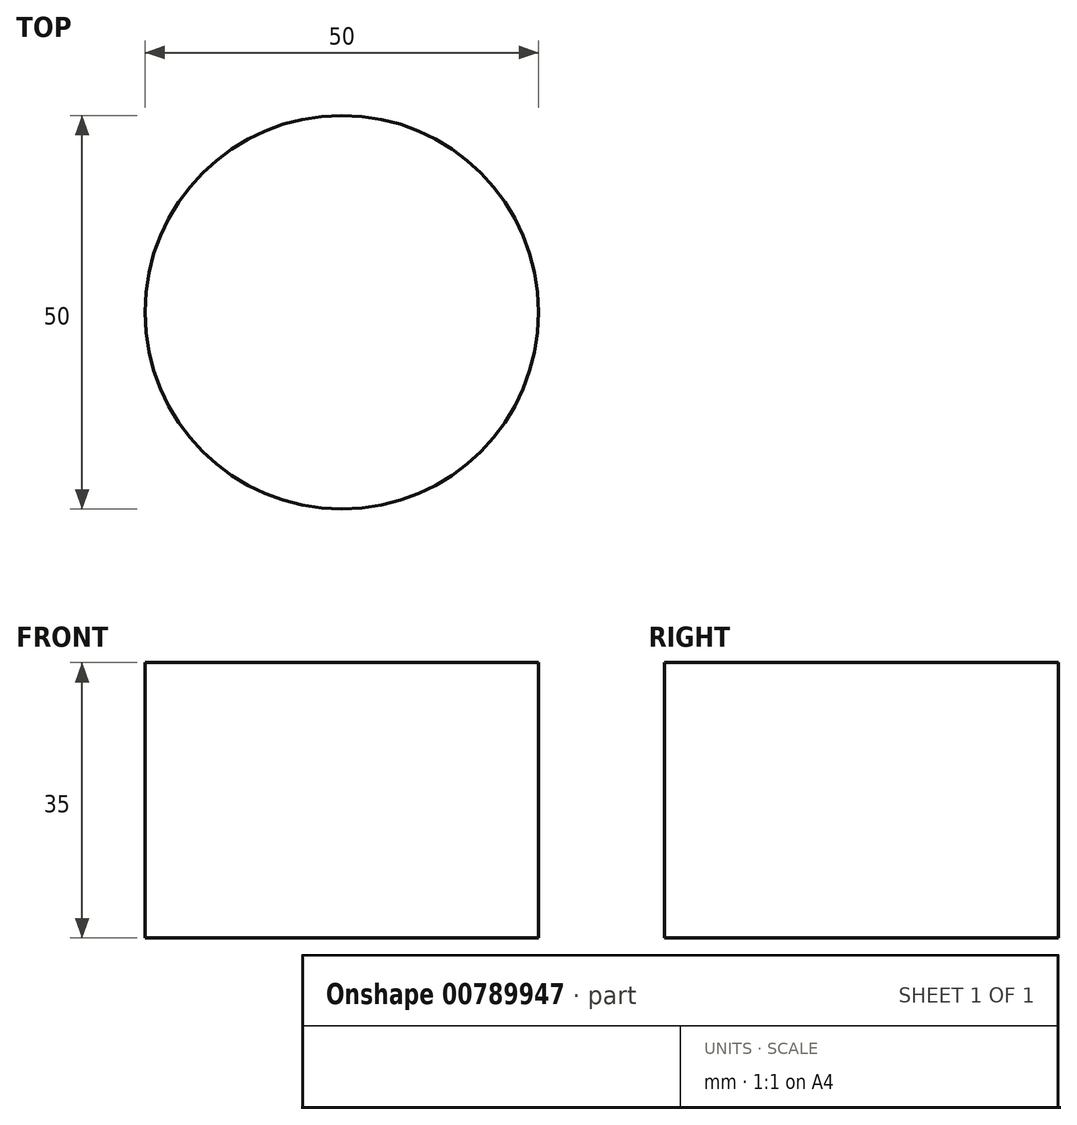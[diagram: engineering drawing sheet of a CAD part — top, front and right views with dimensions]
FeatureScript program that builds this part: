
annotation { "Feature Type Name" : "Feature", "Feature Type Description" : "" }
export const myFeature = defineFeature(function(context is Context, id is Id, definition is map)
    precondition{}
    {
        {
            var Q0;
            Q0=qCreatedBy(makeId("Right.planeOp"),FACE);
            var sketch = newSketch(context, id + "F0", { "sketchPlane" : qUnion([Q0])});
            skLineSegment(sketch, "E0.bottom", {"start": v(0, 0) * mm, "end": v(25, 0) * mm});
            skLineSegment(sketch, "E0.top", {"start": v(0, 35) * mm, "end": v(25, 35) * mm});
            skLineSegment(sketch, "E0.left", {"start": v(0, 0) * mm, "end": v(0, 35) * mm});
            skLineSegment(sketch, "E0.right", {"start": v(25, 0) * mm, "end": v(25, 35) * mm});
            skLineSegment(sketch, "E1", {"start": v(0, -28.57) * mm, "end": v(0, 58.4) * mm, "construction": true});
            skSolve(sketch);
        }
        {
            var Q0;
            Q0=makeQuery(id+"F0.imprint","IMPRINT",FACE,{"disambiguationData":[TD([[makeQuery(id+"F0.imprint","IMPRINT",EDGE,{"derivedFrom":sQuery(id+"F0.wireOp",EDGE,"E0.bottom")}),1.0]])]});
            var Q1;
            Q1=sQuery(id+"F0.wireOp",EDGE,"E1");
            revolve(context, id + "F1", {"surfaceOperationType" : NewSurfaceOperationType.NEW, "entities" : qUnion([Q0]), "axis" : qUnion([Q1]), "revolveType" : RevolveType.FULL});
        }
    });
